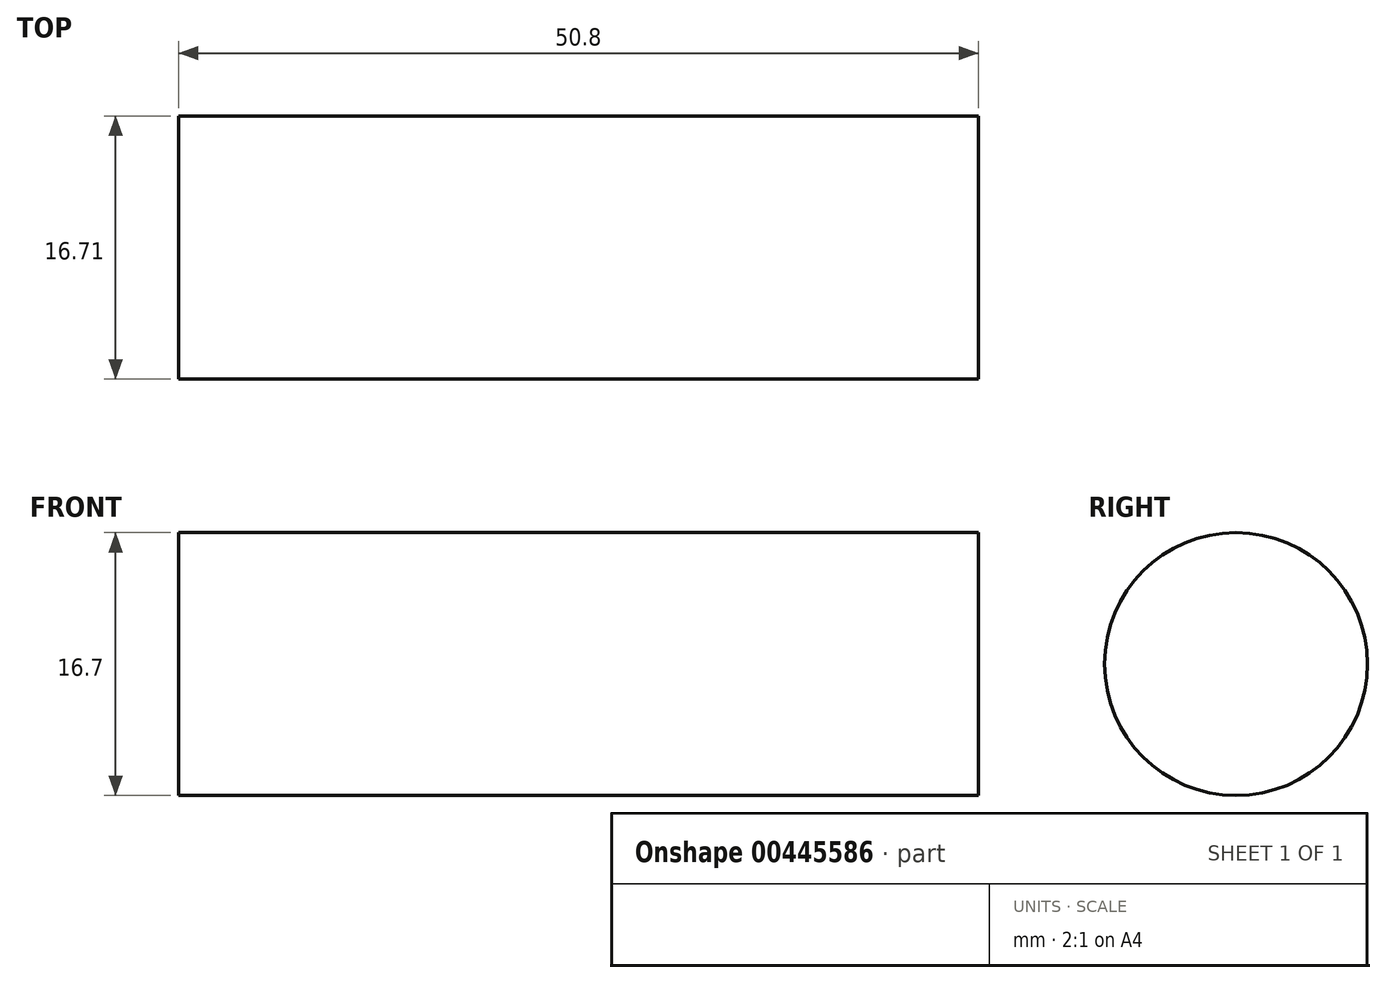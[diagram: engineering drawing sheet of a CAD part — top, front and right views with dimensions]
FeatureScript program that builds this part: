
annotation { "Feature Type Name" : "Feature", "Feature Type Description" : "" }
export const myFeature = defineFeature(function(context is Context, id is Id, definition is map)
    precondition{}
    {
        {
            var Q0;
            Q0=qCreatedBy(makeId("Right.planeOp"),FACE);
            var sketch = newSketch(context, id + "F0", { "sketchPlane" : qUnion([Q0])});
            skCircle(sketch, "E0", {"center": v(-35.45, 28.63) * mm, "radius": 8.35 * mm});
            skSolve(sketch);
        }
        {
            var Q0;
            Q0 = qSketchRegion(id + "F0", true);
            extrude(context, id + "F1", {"entities" : qUnion([Q0]), "depth" : 50.8 * mm});
        }
    });
